# Revit family: Tyco_FireDtctnAlmCtrlIndctEquip_FireClass-AddressableOpticalSmokeHeatAndCODetector
name_source: partatom
category: Fire Alarm Devices
revit_build: Autodesk Revit MEP 2013 (Build: 20120221_2030(x64)
units: mm (PartAtom-declared; Revit-internal decimal feet)

## types (1)
- FC460PC
    AlarmCurrent = 3.3mA
    AssetType = Moveable
    BIMObjectName = Tyco_FireDtctnAlmCtrlIndctEquip_FireClass-AddressableOpticalSmokeHeatAndCODetector-FC460PC
    Brand = FireClass
    Category = Ee_40_15_75
    Color = White
    Default Elevation = 1200 mm
    Description = FireClass-Addressable Optical Smoke, Heat and CO Detector without built in- line isolator and IR Communication Link
    Detector Color = Plastic Material White
    DetectorType = Optical Smoke,Heat and CO Detector
    DeviceBases = 4B_Detector Base/4B-I_Isolator Detector Base
    DurationUnit = Year
    Features = Optical Smoke,Heat and CO Detector
    HasBuiltInAlarm = No
    HasProtectiveEarth = No
    IPCode = IP44
    IfcExportAs = IfcSensorType
    IfcExportType = HEATSENSOR
    IfcTypeObject = IfcBuildingElementProxy
    Manufacturer = Tyco Fire Protection Products
    ManufacturerName = Tyco Fire Protection Products
    ManufacturerURL = www.fireclass.net
    Material = Flame Retardant-FR3010 ‘BAYBLEND'
    Model = FC460PC
    ModelNumber = FC460PC
    NBSDescription = Fire detection and alarm control and indicating equipment (CIE)
    NBSReference = 90-75-30/380
    Name = FC460PC Addressable Optical Smoke, Heat and CO Detector without built in- line isolator and IR Communication Link
    NominalDiameter = 108 mm
    NominalHeight = 42 mm
    NominalLength = 108 mm
    NominalVoltage = 40 V DC
    NominalWidth = 108 mm
    NumberOfPoles = 0
    OperationTemperatureRange = -10 °C to +55 °C
    PhaseAngle = 0.00°
    ProductCodes = 516.460.504
    ProductInformation = https://fireclass.co.uk
    ProductSpecification = FC460PC Addressable Optical Smoke, Heat and CO Detector without built in- line isolator and IR Communication Link
    QuiescentCurrent = 275μA
    RelativeHumidity = 95%(non-condensing)
    ShortCircuitIsolators = No
    StorageTemperature = -20°C to +55 °C
    Type Comments = Only 4B_Detector or 4B-I_Isolator Detector Bases can be used with FC460PC Detector
    URL = https://fireclass.co.uk
    Uniclass2 = Ee_40_15_75
    UsageCurrent = 250μA
    Version = 1
    Voltage = 20 – 40 VDC
    WarrantyDurationLabor = 1.5 years
    WarrantyDurationParts = 1.5 years
    WarrantyDurationUnit = Year
    Weight = (Excluding Base) 94g

## geometry (parser evidence)
native form markers: Blend x2, Sweep x6
no freeform markers — native parametric forms only
